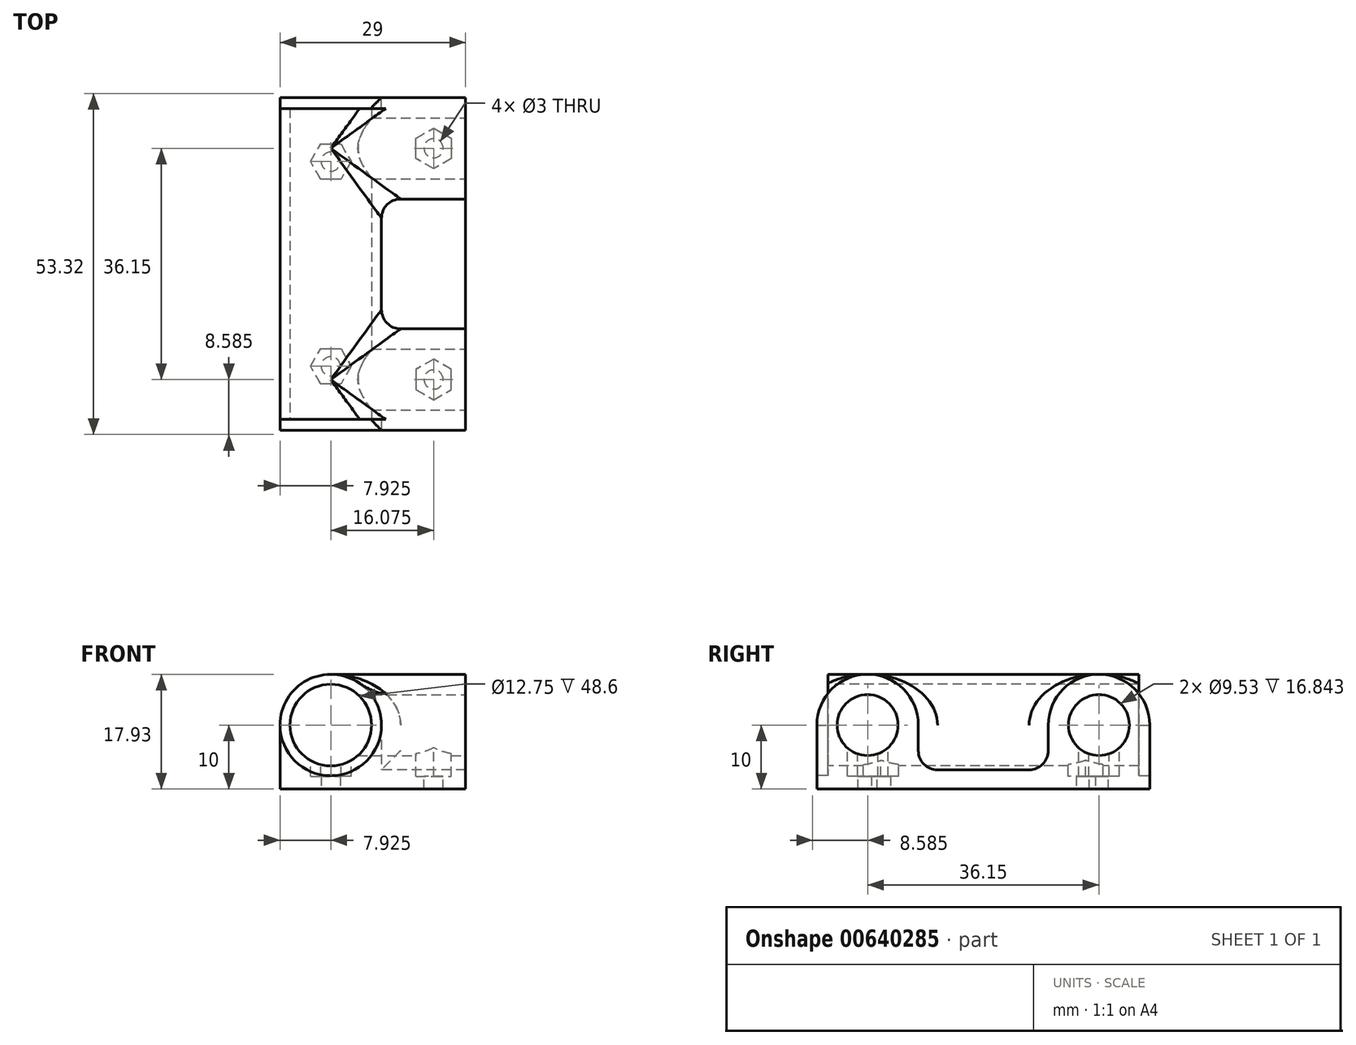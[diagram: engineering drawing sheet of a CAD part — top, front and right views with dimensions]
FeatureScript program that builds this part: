
annotation { "Feature Type Name" : "Feature", "Feature Type Description" : "" }
export const myFeature = defineFeature(function(context is Context, id is Id, definition is map)
    precondition{}
    {
        {
            var Q0;
            Q0=qCreatedBy(makeId("Front.planeOp"),FACE);
            var sketch = newSketch(context, id + "F0", { "sketchPlane" : qUnion([Q0])});
            skLineSegment(sketch, "E0", {"start": v(0, 0) * mm, "end": v(15.85, 0) * mm});
            skLineSegment(sketch, "E1", {"start": v(7.92, 0) * mm, "end": v(7.92, 10) * mm, "construction": true});
            skCircle(sketch, "E2", {"center": v(7.92, 10) * mm, "radius": 7.92 * mm});
            skLineSegment(sketch, "E3", {"start": v(0, 0) * mm, "end": v(0, 10) * mm});
            skLineSegment(sketch, "E4", {"start": v(15.85, 0) * mm, "end": v(15.85, 10) * mm});
            skSolve(sketch);
        }
        {
            var Q0;
            Q0=qSketchRegion(id+"F0",true);
            extrude(context, id + "F1", {"entities" : qUnion([Q0]), "depth" : 52 * mm, "offsetDistance" : 25 * mm});
        }
        {
            var Q0;
            Q0=makeQuery(id+"F1.opExtrude","SWEPT_FACE",FACE,{"disambiguationData":[OSD([sQuery(id+"F0.wireOp",EDGE,"E4")])]});
            var sketch = newSketch(context, id + "F2", { "sketchPlane" : qUnion([Q0])});
            skLineSegment(sketch, "E5.0", {"start": v(-52, 0) * mm, "end": v(0, 0) * mm});
            skLineSegment(sketch, "E6.0", {"start": v(-52, 0) * mm, "end": v(-52, 10) * mm});
            skLineSegment(sketch, "E6.1", {"start": v(0, 0) * mm, "end": v(0, 10) * mm});
            skLineSegment(sketch, "E7", {"start": v(-52, 10) * mm, "end": v(-36.15, 10) * mm, "construction": true});
            skCircle(sketch, "E8", {"center": v(-44.08, 10) * mm, "radius": 7.93 * mm});
            skLineSegment(sketch, "E9", {"start": v(-26, 0) * mm, "end": v(-26, 10) * mm, "construction": true});
            skCircle(sketch, "E10.MirrorC", {"center": v(-7.93, 10) * mm, "radius": 7.93 * mm});
            skLineSegment(sketch, "E11", {"start": v(-36.15, 10) * mm, "end": v(-36.15, 0) * mm});
            skLineSegment(sketch, "E12", {"start": v(-36.15, 0) * mm, "end": v(-36.15, 3) * mm});
            skLineSegment(sketch, "E13", {"start": v(-36.15, 3) * mm, "end": v(-15.85, 3) * mm});
            skLineSegment(sketch, "E14", {"start": v(-15.85, 10) * mm, "end": v(-15.85, 3) * mm});
            skSolve(sketch);
        }
        {
            var Q0;
            Q0=qSketchRegion(id+"F2",true);
            extrude(context, id + "F3", {"entities" : qUnion([Q0]), "operationType" : NewBodyOperationType.ADD, "depth" : (26 - 12.85) * mm, "offsetDistance" : 25 * mm, "hasSecondDirection" : true, "secondDirectionOppositeDirection" : true, "secondDirectionDepth" : (15.85 / 2) * mm});
        }
        {
            var Q0;
            Q0=makeQuery(id+"F3.boolean.opBoolean","MERGE",FACE,{"derivedFrom":[makeQuery(id+"F1.opExtrude","CAP_FACE",FACE,{"disambiguationData":[OSD([sQuery(id+"F0.wireOp",EDGE,"E0"),sQuery(id+"F0.wireOp",EDGE,"E2"),sQuery(id+"F0.wireOp",EDGE,"E3"),sQuery(id+"F0.wireOp",EDGE,"E4")])],"isStart":false}),makeQuery(id+"F3.opExtrude","SWEPT_FACE",FACE,{"disambiguationData":[OSD([sQuery(id+"F2.wireOp",EDGE,"E6.0")])]})]});
            var sketch = newSketch(context, id + "F4", { "sketchPlane" : qUnion([Q0])});
            skArc(sketch, "E15.0", {"start": v(15.85, 10) * mm, "mid": v(7.92, 17.93) * mm, "end": v(0, 10) * mm, "construction": true});
            skCircle(sketch, "E16", {"center": v(7.92, 10) * mm, "radius": 6.38 * mm});
            skSolve(sketch);
        }
        {
            var Q0;
            Q0=qSketchRegion(id+"F4",true);
            extrude(context, id + "F5", {"entities" : qUnion([Q0]), "operationType" : NewBodyOperationType.REMOVE, "oppositeDirection" : true, "depth" : 100 * mm, "offsetDistance" : 25 * mm});
        }
        {
            var Q0;
            Q0=makeQuery(id+"F3.opExtrude","CAP_FACE",FACE,{"disambiguationData":[OSD([sQuery(id+"F2.wireOp",EDGE,"E5.0"),sQuery(id+"F2.wireOp",EDGE,"E6.0"),sQuery(id+"F2.wireOp",EDGE,"E6.1"),sQuery(id+"F2.wireOp",EDGE,"E8"),sQuery(id+"F2.wireOp",EDGE,"E10.MirrorC"),sQuery(id+"F2.wireOp",EDGE,"eMA8j27x-38BE-MHN1-lJ3s-BBI1wRVpQBKV")])],"isStart":false});
            var sketch = newSketch(context, id + "F6", { "sketchPlane" : qUnion([Q0])});
            skLineSegment(sketch, "E17.0", {"start": v(-52, 10) * mm, "end": v(-52, 10) * mm});
            skLineSegment(sketch, "E17.1", {"start": v(0, 10) * mm, "end": v(0, 10) * mm});
            skCircle(sketch, "E18", {"center": v(-44.08, 10) * mm, "radius": 4.76 * mm});
            skCircle(sketch, "E19", {"center": v(-7.93, 10) * mm, "radius": 4.76 * mm});
            skSolve(sketch);
        }
        {
            var Q0;
            Q0=qSketchRegion(id+"F6",true);
            extrude(context, id + "F7", {"entities" : qUnion([Q0]), "operationType" : NewBodyOperationType.REMOVE, "oppositeDirection" : true, "depth" : 20 * mm, "offsetDistance" : 25 * mm});
        }
        {
            var Q0;
            Q0=makeQuery(id+"F3.boolean.opBoolean","MERGE",FACE,{"derivedFrom":[makeQuery(id+"F1.opExtrude","CAP_FACE",FACE,{"disambiguationData":[OSD([sQuery(id+"F0.wireOp",EDGE,"E0"),sQuery(id+"F0.wireOp",EDGE,"E2"),sQuery(id+"F0.wireOp",EDGE,"E3"),sQuery(id+"F0.wireOp",EDGE,"E4")])],"isStart":false}),makeQuery(id+"F3.opExtrude","SWEPT_FACE",FACE,{"disambiguationData":[OSD([sQuery(id+"F2.wireOp",EDGE,"E6.0")])]})]});
            var sketch = newSketch(context, id + "F8", { "sketchPlane" : qUnion([Q0])});
            skCircle(sketch, "E20.0", {"center": v(7.92, 10) * mm, "radius": 6.38 * mm});
            skCircle(sketch, "E21", {"center": v(7.92, 10) * mm, "radius": 7.92 * mm});
            skSolve(sketch);
        }
        {
            var Q0;
            Q0=qSketchRegion(id+"F8",true);
            extrude(context, id + "F9", {"entities" : qUnion([Q0]), "operationType" : NewBodyOperationType.REMOVE, "oppositeDirection" : true, "depth" : 1.7 * mm, "offsetDistance" : 25 * mm});
        }
        {
            var Q0;
            Q0=makeQuery(id+"F3.boolean.opBoolean","MERGE",FACE,{"derivedFrom":[makeQuery(id+"F1.opExtrude","CAP_FACE",FACE,{"disambiguationData":[OSD([sQuery(id+"F0.wireOp",EDGE,"E0"),sQuery(id+"F0.wireOp",EDGE,"E2"),sQuery(id+"F0.wireOp",EDGE,"E3"),sQuery(id+"F0.wireOp",EDGE,"E4")])],"isStart":true}),makeQuery(id+"F3.opExtrude","SWEPT_FACE",FACE,{"disambiguationData":[OSD([sQuery(id+"F2.wireOp",EDGE,"E6.1")])]})]});
            var sketch = newSketch(context, id + "F10", { "sketchPlane" : qUnion([Q0])});
            skCircle(sketch, "E22.0", {"center": v(-7.92, 10) * mm, "radius": 6.38 * mm});
            skCircle(sketch, "E23", {"center": v(-7.92, 10) * mm, "radius": 7.92 * mm});
            skSolve(sketch);
        }
        {
            var Q0;
            Q0=qSketchRegion(id+"F10",true);
            extrude(context, id + "F11", {"entities" : qUnion([Q0]), "operationType" : NewBodyOperationType.REMOVE, "oppositeDirection" : true, "depth" : 1.7 * mm, "offsetDistance" : 25 * mm});
        }
        {
            var Q0;
            Q0=qCreatedBy(makeId("Top.planeOp"),FACE);
            var sketch = newSketch(context, id + "F12", { "sketchPlane" : qUnion([Q0])});
            skPoint(sketch, "E24.0", {"position": v(0, -52) * mm});
            skPoint(sketch, "E24.1", {"position": v(29, 0) * mm});
            skLineSegment(sketch, "E25.bottom", {"start": v(29, 0) * mm, "end": v(0, 0) * mm, "construction": true});
            skLineSegment(sketch, "E25.top", {"start": v(29, -52) * mm, "end": v(0, -52) * mm, "construction": true});
            skLineSegment(sketch, "E25.left", {"start": v(29, 0) * mm, "end": v(29, -52) * mm, "construction": true});
            skLineSegment(sketch, "E25.right", {"start": v(0, 0) * mm, "end": v(0, -52) * mm, "construction": true});
            skLineSegment(sketch, "E26", {"start": v(14.5, -52) * mm, "end": v(14.5, -42) * mm, "construction": true});
            skPoint(sketch, "E26.endSnap0", {"position": v(14.5, -52) * mm});
            skCircle(sketch, "E27", {"center": v(24, -42) * mm, "radius": 1.5 * mm, "construction": true});
            skCircle(sketch, "E28", {"center": v(7.92, -42) * mm, "radius": 1.5 * mm});
            skLineSegment(sketch, "E29", {"start": v(0, -26) * mm, "end": v(13.04, -26) * mm, "construction": true});
            skCircle(sketch, "E30.MirrorC", {"center": v(7.92, -10) * mm, "radius": 1.5 * mm});
            skCircle(sketch, "E31.MirrorC", {"center": v(24, -10) * mm, "radius": 1.5 * mm, "construction": true});
            skLineSegment(sketch, "E32", {"start": v(24, -42) * mm, "end": v(24, -10) * mm, "construction": true});
            skLineSegment(sketch, "E33", {"start": v(7.92, -42) * mm, "end": v(0, -42) * mm, "construction": true});
            skLineSegment(sketch, "E34", {"start": v(24, -42) * mm, "end": v(29, -42) * mm, "construction": true});
            skSolve(sketch);
        }
        {
            var Q0;
            Q0=qSketchRegion(id+"F12",true);
            extrude(context, id + "F13", {"entities" : qUnion([Q0]), "operationType" : NewBodyOperationType.REMOVE, "depth" : 10 * mm, "offsetDistance" : 25 * mm});
        }
        {
            var Q0;
            Q0=makeQuery(id+"F3.boolean.opBoolean","INTERSECT",EDGE,{"derivedFrom":[makeQuery(id+"F1.opExtrude","SWEPT_FACE",FACE,{"disambiguationData":[OSD([sQuery(id+"F0.wireOp",EDGE,"E4")])]}),makeQuery(id+"F3.opExtrude","SWEPT_FACE",FACE,{"disambiguationData":[OSD([sQuery(id+"F2.wireOp",EDGE,"E11")])]})]});
            var Q1;
            Q1=makeQuery(id+"F3.boolean.opBoolean","INTERSECT",EDGE,{"disambiguationData":[OD(1.0)],"derivedFrom":[makeQuery(id+"F1.opExtrude","SWEPT_FACE",FACE,{"disambiguationData":[OSD([sQuery(id+"F0.wireOp",EDGE,"E2")])]}),makeQuery(id+"F3.opExtrude","SWEPT_FACE",FACE,{"disambiguationData":[OSD([sQuery(id+"F2.wireOp",EDGE,"E8")])]})]});
            var Q2;
            Q2=makeQuery(id+"F3.opExtrude","SWEPT_EDGE",EDGE,{"disambiguationData":[OSD([sQuery(id+"F2.wireOp",EDGE,"E11"),sQuery(id+"F2.wireOp",EDGE,"E12"),sQuery(id+"F2.wireOp",EDGE,"E13")])]});
            var Q3;
            Q3=makeQuery(id+"F3.opExtrude","SWEPT_EDGE",EDGE,{"disambiguationData":[OSD([sQuery(id+"F2.wireOp",EDGE,"E13"),sQuery(id+"F2.wireOp",EDGE,"E14")])]});
            var Q4;
            Q4=makeQuery(id+"F3.boolean.opBoolean","INTERSECT",EDGE,{"derivedFrom":[makeQuery(id+"F1.opExtrude","SWEPT_FACE",FACE,{"disambiguationData":[OSD([sQuery(id+"F0.wireOp",EDGE,"E4")])]}),makeQuery(id+"F3.opExtrude","SWEPT_FACE",FACE,{"disambiguationData":[OSD([sQuery(id+"F2.wireOp",EDGE,"E14")])]})]});
            var Q5;
            Q5=makeQuery(id+"F3.boolean.opBoolean","INTERSECT",EDGE,{"disambiguationData":[OD(1.0)],"derivedFrom":[makeQuery(id+"F1.opExtrude","SWEPT_FACE",FACE,{"disambiguationData":[OSD([sQuery(id+"F0.wireOp",EDGE,"E2")])]}),makeQuery(id+"F3.opExtrude","SWEPT_FACE",FACE,{"disambiguationData":[OSD([sQuery(id+"F2.wireOp",EDGE,"E10.MirrorC")])]})]});
            var Q6;
            {var subQ0=makeQuery(id+"F1.opExtrude","SWEPT_FACE",FACE,{"disambiguationData":[OSD([sQuery(id+"F0.wireOp",EDGE,"E2")])]});var subQ1=makeQuery(id+"F3.opExtrude","SWEPT_FACE",FACE,{"disambiguationData":[OSD([sQuery(id+"F2.wireOp",EDGE,"E8")])]});Q6=makeQuery(id+"F9.boolean.opBoolean","SPLIT",EDGE,{"disambiguationData":[topologyDisambiguationEdgeConnected([subQ0])],"derivedFrom":makeQuery(id+"F3.boolean.opBoolean","INTERSECT",EDGE,{"disambiguationData":[OD(0.0)],"derivedFrom":[subQ0,subQ1]})});}
            var Q7;
            {var subQ0=makeQuery(id+"F1.opExtrude","SWEPT_FACE",FACE,{"disambiguationData":[OSD([sQuery(id+"F0.wireOp",EDGE,"E2")])]});var subQ1=makeQuery(id+"F3.opExtrude","SWEPT_FACE",FACE,{"disambiguationData":[OSD([sQuery(id+"F2.wireOp",EDGE,"E10.MirrorC")])]});Q7=makeQuery(id+"F11.boolean.opBoolean","SPLIT",EDGE,{"disambiguationData":[topologyDisambiguationEdgeConnected([subQ0])],"derivedFrom":makeQuery(id+"F3.boolean.opBoolean","INTERSECT",EDGE,{"disambiguationData":[OD(0.0)],"derivedFrom":[subQ0,subQ1]})});}
            fillet(context, id + "F14", {"entities" : qUnion([Q0, Q1, Q2, Q3, Q4, Q5, Q6, Q7]), "radius" : 3 * mm, "tangentPropagation" : true, "allowEdgeOverflow" : false});
        }
        {
            var Q0;
            Q0=qCreatedBy(makeId("Top.planeOp"),FACE);
            cPlane(context, id + "F15", {"entities" : qUnion([Q0]), "cplaneType" : CPlaneType.OFFSET, "offset" : 10 * mm, "width" : 150 * mm, "height" : 150 * mm});
        }
        {
            var Q0;
            Q0=qCreatedBy(id+"F15.planeOp",FACE);
            var sketch = newSketch(context, id + "F16", { "sketchPlane" : qUnion([Q0])});
            skPoint(sketch, "E35.0", {"position": v(29, -7.92) * mm});
            skPoint(sketch, "E35.1", {"position": v(29, -44.08) * mm});
            skLineSegment(sketch, "E36", {"start": v(29, -7.92) * mm, "end": v(24, -7.92) * mm, "construction": true});
            skCircle(sketch, "E37.cCircle", {"center": v(24, -7.92) * mm, "radius": 2.75 * mm, "construction": true});
            skLineSegment(sketch, "E37.0", {"start": v(26.75, -6.34) * mm, "end": v(26.75, -9.51) * mm});
            skLineSegment(sketch, "E37.1", {"start": v(26.75, -9.51) * mm, "end": v(24, -11.1) * mm});
            skLineSegment(sketch, "E37.2", {"start": v(24, -11.1) * mm, "end": v(21.25, -9.51) * mm});
            skLineSegment(sketch, "E37.3", {"start": v(21.25, -9.51) * mm, "end": v(21.25, -6.34) * mm});
            skLineSegment(sketch, "E37.4", {"start": v(21.25, -6.34) * mm, "end": v(24, -4.75) * mm});
            skLineSegment(sketch, "E37.5", {"start": v(24, -4.75) * mm, "end": v(26.75, -6.34) * mm});
            skPoint(sketch, "E37.0.midPoint", {"position": v(26.75, -7.92) * mm});
            skPoint(sketch, "E38.0", {"position": v(29, -26) * mm});
            skLineSegment(sketch, "E39", {"start": v(29, -26) * mm, "end": v(17.5, -26) * mm, "construction": true});
            skLineSegment(sketch, "E40.MirrorCS", {"start": v(24, -47.25) * mm, "end": v(26.75, -45.66) * mm});
            skLineSegment(sketch, "E41.MirrorCS", {"start": v(21.25, -45.66) * mm, "end": v(24, -47.25) * mm});
            skLineSegment(sketch, "E42.MirrorCS", {"start": v(21.25, -42.49) * mm, "end": v(21.25, -45.66) * mm});
            skLineSegment(sketch, "E43.MirrorCS", {"start": v(24, -40.9) * mm, "end": v(21.25, -42.49) * mm});
            skLineSegment(sketch, "E44.MirrorCS", {"start": v(26.75, -42.49) * mm, "end": v(24, -40.9) * mm});
            skLineSegment(sketch, "E45.MirrorCS", {"start": v(26.75, -45.66) * mm, "end": v(26.75, -42.49) * mm});
            skCircle(sketch, "E46.0", {"center": v(7.92, -42) * mm, "radius": 1.5 * mm, "construction": true});
            skCircle(sketch, "E46.1", {"center": v(7.92, -10) * mm, "radius": 1.5 * mm, "construction": true});
            skCircle(sketch, "E47.cCircle", {"center": v(7.92, -10) * mm, "radius": 2.75 * mm, "construction": true});
            skLineSegment(sketch, "E47.0", {"start": v(11.1, -10) * mm, "end": v(9.51, -12.75) * mm});
            skLineSegment(sketch, "E47.1", {"start": v(9.51, -12.75) * mm, "end": v(6.34, -12.75) * mm});
            skLineSegment(sketch, "E47.2", {"start": v(6.34, -12.75) * mm, "end": v(4.75, -10) * mm});
            skLineSegment(sketch, "E47.3", {"start": v(4.75, -10) * mm, "end": v(6.34, -7.25) * mm});
            skLineSegment(sketch, "E47.4", {"start": v(6.34, -7.25) * mm, "end": v(9.51, -7.25) * mm});
            skLineSegment(sketch, "E47.5", {"start": v(9.51, -7.25) * mm, "end": v(11.1, -10) * mm});
            skPoint(sketch, "E47.0.midPoint", {"position": v(10.3, -11.38) * mm});
            skCircle(sketch, "E48.cCircle", {"center": v(7.92, -42) * mm, "radius": 2.75 * mm, "construction": true});
            skLineSegment(sketch, "E48.0", {"start": v(11.1, -42) * mm, "end": v(9.51, -44.75) * mm});
            skLineSegment(sketch, "E48.1", {"start": v(9.51, -44.75) * mm, "end": v(6.34, -44.75) * mm});
            skLineSegment(sketch, "E48.2", {"start": v(6.34, -44.75) * mm, "end": v(4.75, -42) * mm});
            skLineSegment(sketch, "E48.3", {"start": v(4.75, -42) * mm, "end": v(6.34, -39.25) * mm});
            skLineSegment(sketch, "E48.4", {"start": v(6.34, -39.25) * mm, "end": v(9.51, -39.25) * mm});
            skLineSegment(sketch, "E48.5", {"start": v(9.51, -39.25) * mm, "end": v(11.1, -42) * mm});
            skPoint(sketch, "E48.0.midPoint", {"position": v(10.3, -43.37) * mm});
            skSolve(sketch);
        }
        {
            var Q0;
            Q0=qSketchRegion(id+"F16",true);
            extrude(context, id + "F17", {"entities" : qUnion([Q0]), "operationType" : NewBodyOperationType.REMOVE, "oppositeDirection" : true, "depth" : 8 * mm, "offsetDistance" : 25 * mm});
        }
        {
            var Q0;
            Q0=makeQuery(id+"F17.boolean.opBoolean","COPY",FACE,{"derivedFrom":makeQuery(id+"F17.opExtrude","CAP_FACE",FACE,{"disambiguationData":[OSD([sQuery(id+"F16.wireOp",EDGE,"E37.0"),sQuery(id+"F16.wireOp",EDGE,"E37.1"),sQuery(id+"F16.wireOp",EDGE,"E37.2"),sQuery(id+"F16.wireOp",EDGE,"E37.3"),sQuery(id+"F16.wireOp",EDGE,"E37.4"),sQuery(id+"F16.wireOp",EDGE,"E37.5")])],"isStart":false})});
            var sketch = newSketch(context, id + "F18", { "sketchPlane" : qUnion([Q0])});
            skPoint(sketch, "E49.0", {"position": v(24, -4.75) * mm});
            skPoint(sketch, "E49.1", {"position": v(24, -11.1) * mm});
            skLineSegment(sketch, "E50", {"start": v(24, -4.75) * mm, "end": v(24, -11.1) * mm, "construction": true});
            skCircle(sketch, "E51", {"center": v(24, -7.93) * mm, "radius": 1.5 * mm});
            skPoint(sketch, "E52.0", {"position": v(29, -26) * mm});
            skLineSegment(sketch, "E53", {"start": v(29, -26) * mm, "end": v(24.33, -26) * mm, "construction": true});
            skCircle(sketch, "E54.MirrorC", {"center": v(24, -44.07) * mm, "radius": 1.5 * mm});
            skSolve(sketch);
        }
        {
            var Q0;
            Q0=qSketchRegion(id+"F18",true);
            extrude(context, id + "F19", {"entities" : qUnion([Q0]), "operationType" : NewBodyOperationType.REMOVE, "oppositeDirection" : true, "depth" : 25 * mm, "offsetDistance" : 25 * mm});
        }
    });
